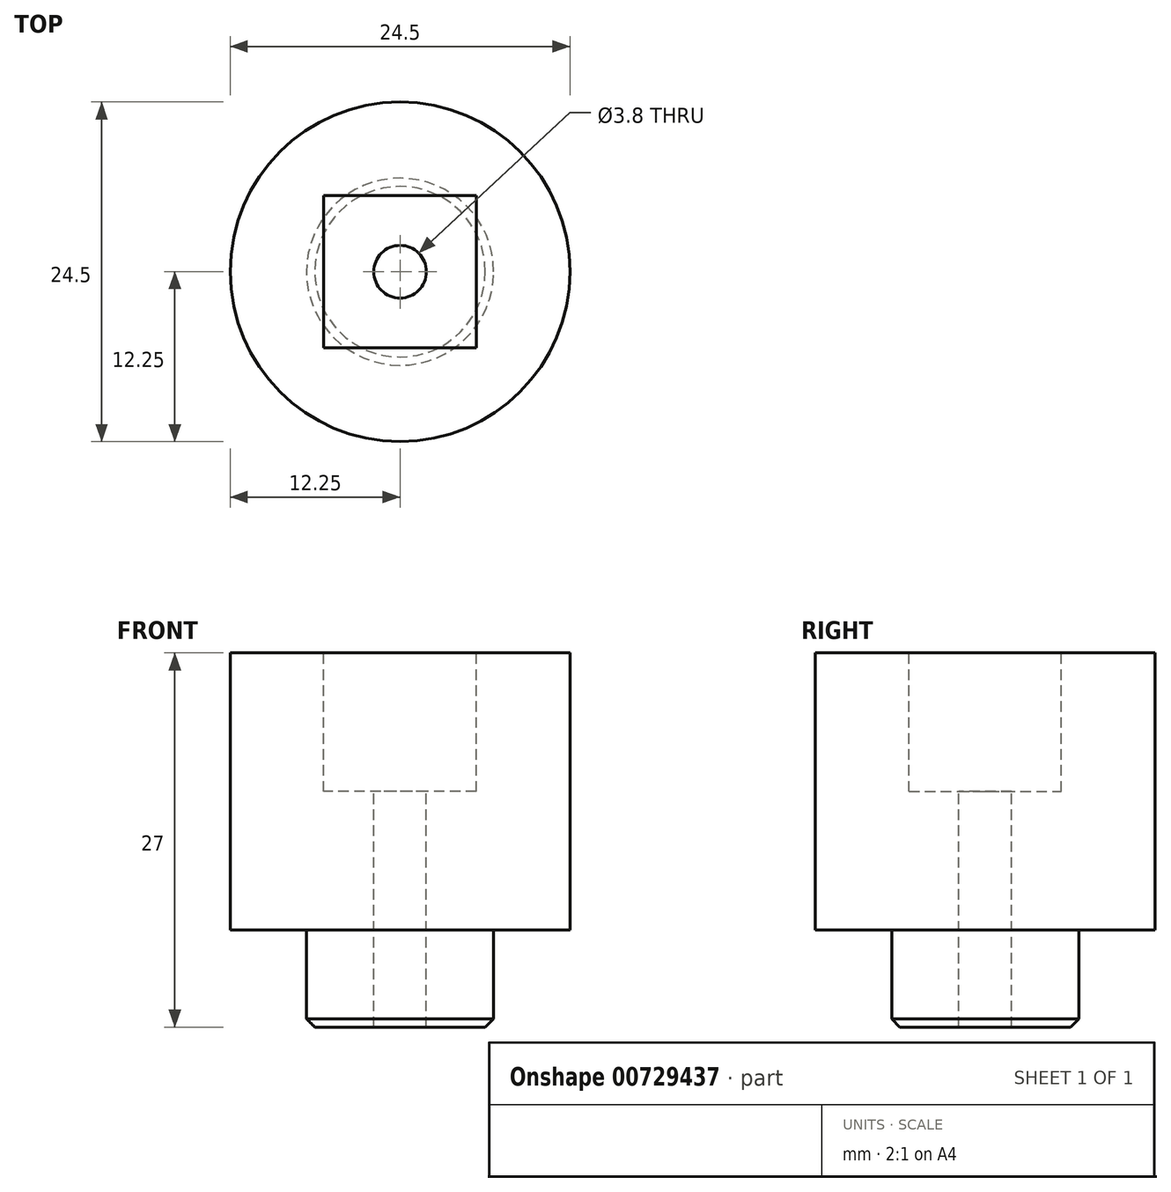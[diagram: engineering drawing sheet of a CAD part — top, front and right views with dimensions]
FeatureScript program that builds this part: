
annotation { "Feature Type Name" : "Feature", "Feature Type Description" : "" }
export const myFeature = defineFeature(function(context is Context, id is Id, definition is map)
    precondition{}
    {
        {
            var Q0;
            Q0=qCreatedBy(makeId("Top.planeOp"),FACE);
            var sketch = newSketch(context, id + "F0", { "sketchPlane" : qUnion([Q0])});
            skCircle(sketch, "E0", {"center": v(0, 0) * mm, "radius": 12.25 * mm});
            skSolve(sketch);
        }
        {
            var Q0;
            Q0=makeQuery(id+"F0.imprint","IMPRINT",FACE,{"disambiguationData":[TD([[makeQuery(id+"F0.imprint","IMPRINT",EDGE,{"derivedFrom":sQuery(id+"F0.wireOp",EDGE,"E0")}),1.0]])]});
            extrude(context, id + "F1", {"entities" : qUnion([Q0]), "depth" : 20 * mm, "offsetDistance" : 25 * mm});
        }
        {
            var Q0;
            Q0=makeQuery(id+"F1.opExtrude","CAP_FACE",FACE,{"disambiguationData":[OSD([sQuery(id+"F0.wireOp",EDGE,"E0")])],"isStart":false});
            var sketch = newSketch(context, id + "F2", { "sketchPlane" : qUnion([Q0])});
            skLineSegment(sketch, "E1.bottom", {"start": v(5.5, -5.5) * mm, "end": v(-5.5, -5.5) * mm});
            skLineSegment(sketch, "E1.top", {"start": v(5.5, 5.5) * mm, "end": v(-5.5, 5.5) * mm});
            skLineSegment(sketch, "E1.left", {"start": v(5.5, -5.5) * mm, "end": v(5.5, 5.5) * mm});
            skLineSegment(sketch, "E1.right", {"start": v(-5.5, -5.5) * mm, "end": v(-5.5, 5.5) * mm});
            skPoint(sketch, "E1.middle", {"position": v(0, 0) * mm});
            skSolve(sketch);
        }
        {
            var Q0;
            Q0=makeQuery(id+"F2.imprint","IMPRINT",FACE,{"disambiguationData":[TD([[makeQuery(id+"F2.imprint","IMPRINT",EDGE,{"derivedFrom":sQuery(id+"F2.wireOp",EDGE,"E1.bottom")}),-1.0]])]});
            extrude(context, id + "F3", {"entities" : qUnion([Q0]), "operationType" : NewBodyOperationType.REMOVE, "oppositeDirection" : true, "depth" : 10 * mm, "offsetDistance" : 25 * mm});
        }
        {
            var Q0;
            Q0=makeQuery(id+"F3.boolean.opBoolean","COPY",FACE,{"derivedFrom":makeQuery(id+"F3.opExtrude","CAP_FACE",FACE,{"disambiguationData":[OSD([sQuery(id+"F2.wireOp",EDGE,"E1.bottom"),sQuery(id+"F2.wireOp",EDGE,"E1.top"),sQuery(id+"F2.wireOp",EDGE,"E1.left"),sQuery(id+"F2.wireOp",EDGE,"E1.right")])],"isStart":false})});
            var sketch = newSketch(context, id + "F4", { "sketchPlane" : qUnion([Q0])});
            skCircle(sketch, "E2", {"center": v(0, 0) * mm, "radius": 1.9 * mm});
            skSolve(sketch);
        }
        {
            var Q0;
            Q0=makeQuery(id+"F4.imprint","IMPRINT",FACE,{"disambiguationData":[TD([[makeQuery(id+"F4.imprint","IMPRINT",EDGE,{"derivedFrom":sQuery(id+"F4.wireOp",EDGE,"E2")}),1.0]])]});
            extrude(context, id + "F5", {"entities" : qUnion([Q0]), "operationType" : NewBodyOperationType.REMOVE, "oppositeDirection" : true, "depth" : 40 * mm, "offsetDistance" : 25 * mm});
        }
        {
            var Q0;
            Q0=makeQuery(id+"F1.opExtrude","CAP_FACE",FACE,{"disambiguationData":[OSD([sQuery(id+"F0.wireOp",EDGE,"E0")])],"isStart":true});
            var sketch = newSketch(context, id + "F6", { "sketchPlane" : qUnion([Q0])});
            skCircle(sketch, "E3", {"center": v(0, 0) * mm, "radius": 6.75 * mm});
            skSolve(sketch);
        }
        {
            var Q0;
            Q0=makeQuery(id+"F6.imprint","IMPRINT",FACE,{"disambiguationData":[TD([[makeQuery(id+"F6.imprint","IMPRINT",EDGE,{"derivedFrom":sQuery(id+"F6.wireOp",EDGE,"E3")}),1.0]])]});
            extrude(context, id + "F7", {"entities" : qUnion([Q0]), "operationType" : NewBodyOperationType.ADD, "depth" : 7 * mm, "offsetDistance" : 25 * mm});
        }
        {
            var Q0;
            Q0=makeQuery(id+"F7.opExtrude","CAP_EDGE",EDGE,{"disambiguationData":[OSD([sQuery(id+"F6.wireOp",EDGE,"E3")])],"isStart":false});
            chamfer(context, id + "F8", {"entities" : qUnion([Q0]), "width" : 0.6 * mm, "tangentPropagation" : true});
        }
    });
